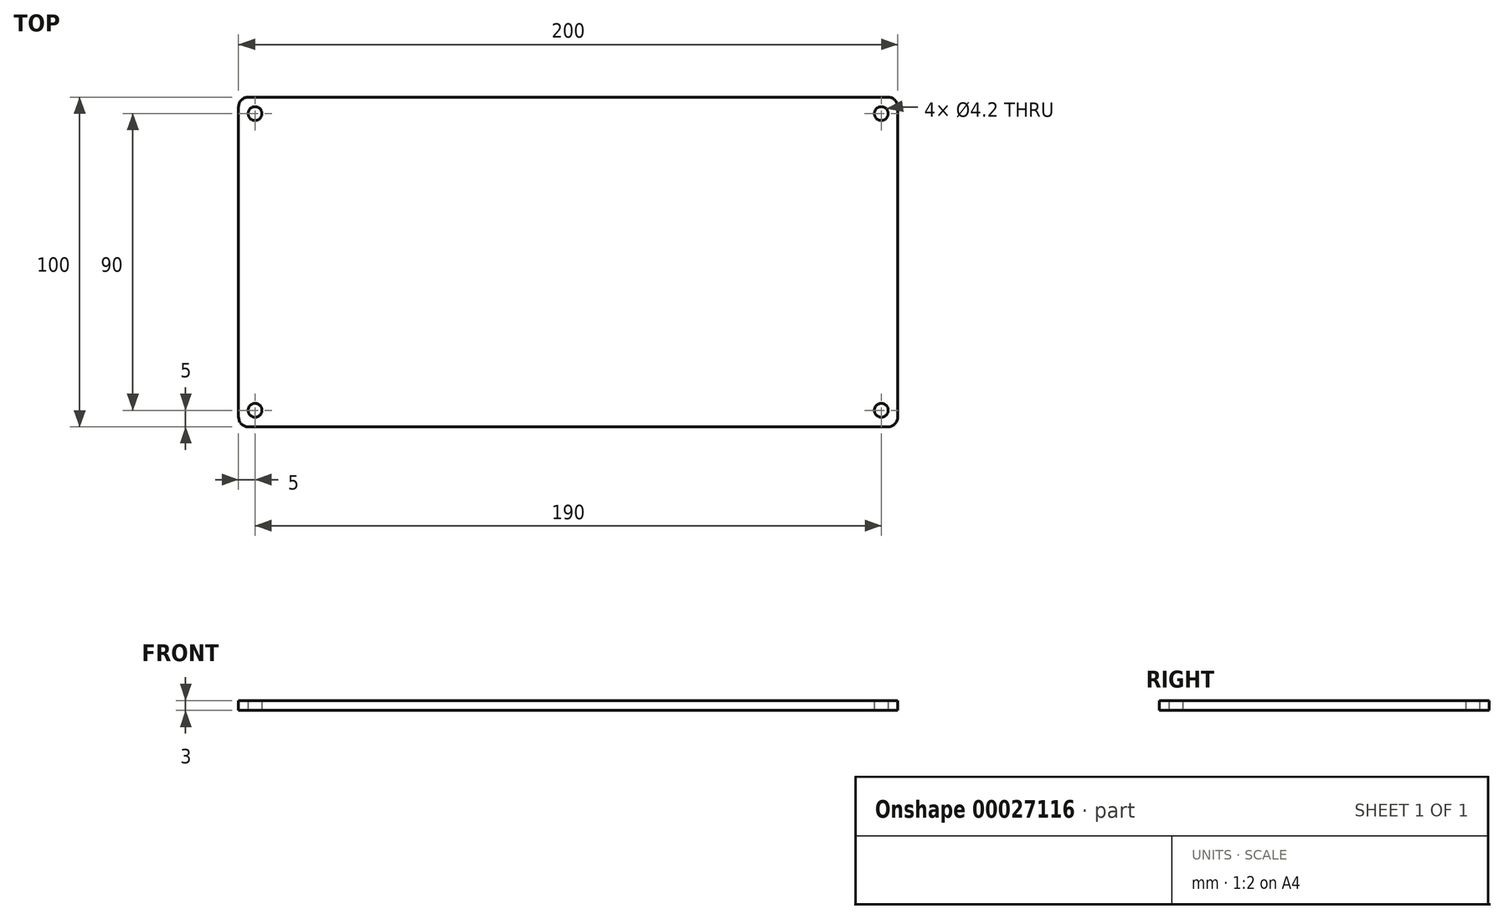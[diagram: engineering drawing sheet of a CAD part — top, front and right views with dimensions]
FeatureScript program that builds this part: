
annotation { "Feature Type Name" : "Feature", "Feature Type Description" : "" }
export const myFeature = defineFeature(function(context is Context, id is Id, definition is map)
    precondition{}
    {
        {
            var Q0;
            Q0=qCreatedBy(makeId("Top.planeOp"),FACE);
            var sketch = newSketch(context, id + "F0", { "sketchPlane" : qUnion([Q0])});
            skLineSegment(sketch, "E0.rect.bottom", {"start": v(100, -50) * mm, "end": v(-100, -50) * mm});
            skLineSegment(sketch, "E0.rect.top", {"start": v(100, 50) * mm, "end": v(-100, 50) * mm});
            skLineSegment(sketch, "E0.rect.left", {"start": v(100, -50) * mm, "end": v(100, 50) * mm});
            skLineSegment(sketch, "E0.rect.right", {"start": v(-100, -50) * mm, "end": v(-100, 50) * mm});
            skLineSegment(sketch, "E1.0", {"start": v(95, 45) * mm, "end": v(-95, 45) * mm, "construction": true});
            skLineSegment(sketch, "E1.1", {"start": v(95, -45) * mm, "end": v(95, 45) * mm, "construction": true});
            skLineSegment(sketch, "E1.2", {"start": v(95, -45) * mm, "end": v(-95, -45) * mm, "construction": true});
            skLineSegment(sketch, "E1.3", {"start": v(-95, -45) * mm, "end": v(-95, 45) * mm, "construction": true});
            skCircle(sketch, "E2", {"center": v(-95, 45) * mm, "radius": 2.1 * mm});
            skCircle(sketch, "E3.MirrorC", {"center": v(95, 45) * mm, "radius": 2.1 * mm});
            skCircle(sketch, "E4.MirrorC", {"center": v(-95, -45) * mm, "radius": 2.1 * mm});
            skCircle(sketch, "E5.MirrorC", {"center": v(95, -45) * mm, "radius": 2.1 * mm});
            skSolve(sketch);
        }
        {
            var Q0;
            Q0=makeQuery(id+"F0.imprint","IMPRINT",FACE,{"disambiguationData":[TD([[makeQuery(id+"F0.imprint","IMPRINT",EDGE,{"derivedFrom":sQuery(id+"F0.wireOp",EDGE,"E0.rect.bottom")}),-1.0]])]});
            extrude(context, id + "F1", {"entities" : qUnion([Q0]), "depth" : 3 * mm});
        }
        {
            var Q0;
            Q0=makeQuery(id+"F1.opExtrude","SWEPT_EDGE",EDGE,{"disambiguationData":[OSD([sQuery(id+"F0.wireOp",EDGE,"E0.rect.top"),sQuery(id+"F0.wireOp",EDGE,"E0.rect.left")])]});
            var Q1;
            Q1=makeQuery(id+"F1.opExtrude","SWEPT_EDGE",EDGE,{"disambiguationData":[OSD([sQuery(id+"F0.wireOp",EDGE,"E0.rect.bottom"),sQuery(id+"F0.wireOp",EDGE,"E0.rect.left")])]});
            var Q2;
            Q2=makeQuery(id+"F1.opExtrude","SWEPT_EDGE",EDGE,{"disambiguationData":[OSD([sQuery(id+"F0.wireOp",EDGE,"E0.rect.bottom"),sQuery(id+"F0.wireOp",EDGE,"E0.rect.right")])]});
            var Q3;
            Q3=makeQuery(id+"F1.opExtrude","SWEPT_EDGE",EDGE,{"disambiguationData":[OSD([sQuery(id+"F0.wireOp",EDGE,"E0.rect.top"),sQuery(id+"F0.wireOp",EDGE,"E0.rect.right")])]});
            fillet(context, id + "F2", {"entities" : qUnion([Q0, Q1, Q2, Q3]), "radius" : 3 * mm, "tangentPropagation" : true, "allowEdgeOverflow" : false});
        }
    });
